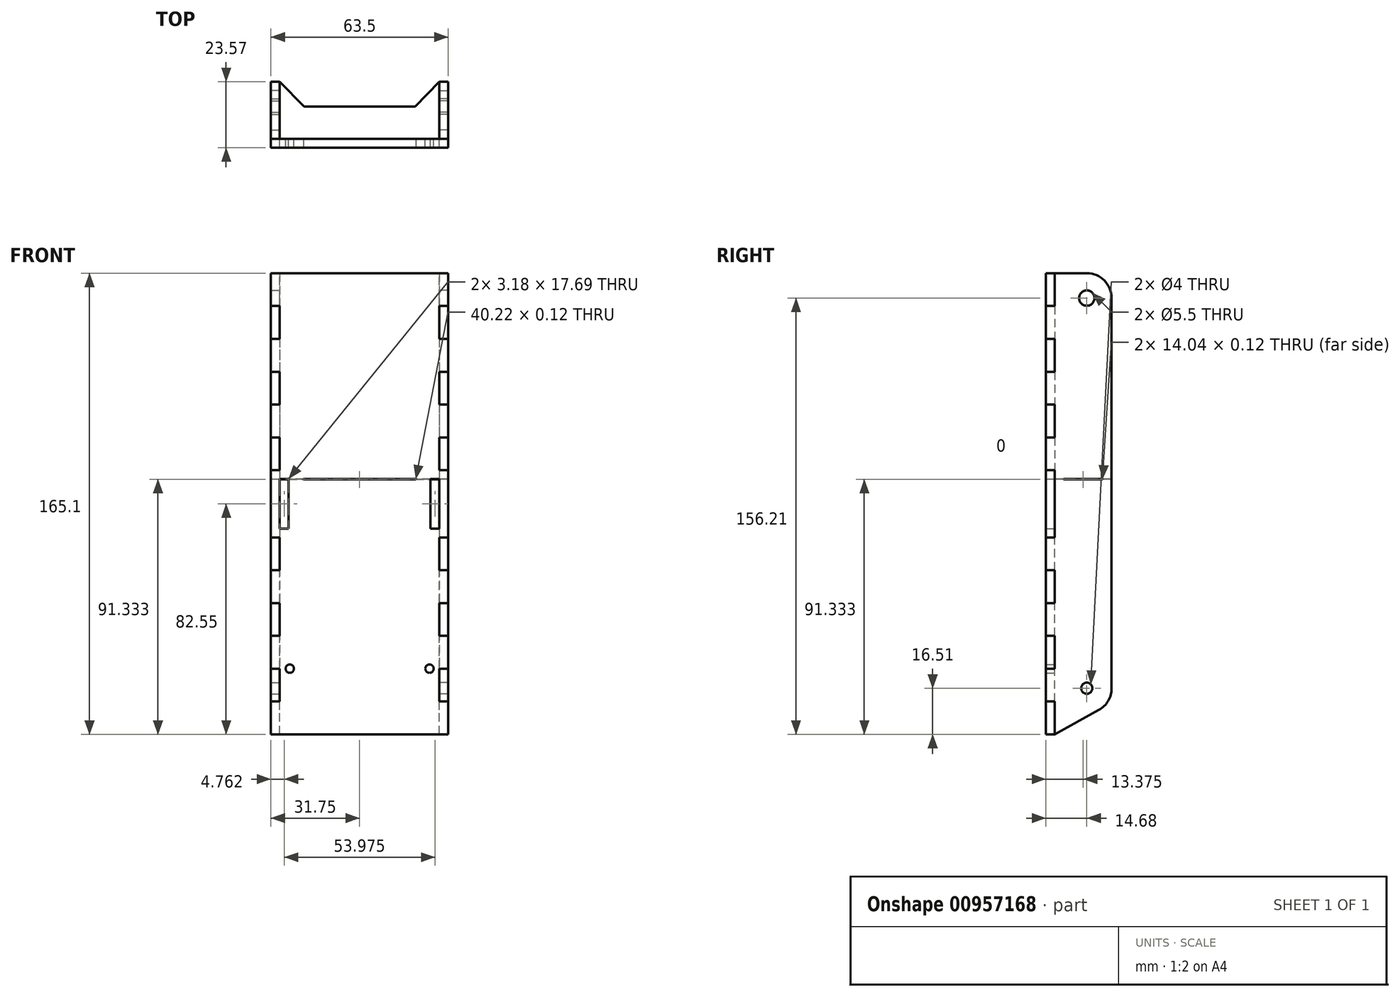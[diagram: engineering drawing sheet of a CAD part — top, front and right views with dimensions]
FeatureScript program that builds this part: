
annotation { "Feature Type Name" : "Feature", "Feature Type Description" : "" }
export const myFeature = defineFeature(function(context is Context, id is Id, definition is map)
    precondition{}
    {
        {
            assignVariable(context, id + "F0", {"name" : "Thickness", "anyValue" : .125});
        }
        {
            var Q0;
            Q0=qCreatedBy(makeId("Front.planeOp"),FACE);
            var sketch = newSketch(context, id + "F1", { "sketchPlane" : qUnion([Q0])});
            skLineSegment(sketch, "E0", {"start": v(0, 0) * mm, "end": v(0, 49.56) * mm, "construction": true});
            skLineSegment(sketch, "E1", {"start": v(0, 0) * mm, "end": v(-25, 0) * mm, "construction": true});
            skCircle(sketch, "E2", {"center": v(-25, 0) * mm, "radius": 1.5 * mm, "construction": true});
            skLineSegment(sketch, "E3", {"start": v(0, -7) * mm, "end": v(-39.83, -7) * mm, "construction": true});
            skLineSegment(sketch, "E4", {"start": v(0, 141.6) * mm, "end": v(-22.22, 141.6) * mm, "construction": true});
            skLineSegment(sketch, "E5", {"start": v(-22.23, 141.6) * mm, "end": v(-22.22, -23.51) * mm, "construction": true});
            skLineSegment(sketch, "E6", {"start": v(-22.22, -23.51) * mm, "end": v(0, -23.5) * mm, "construction": true});
            skSolve(sketch);
        }
        {
            var Q0;
            Q0=qCreatedBy(makeId("Right.planeOp"),FACE);
            var sketch = newSketch(context, id + "F2", { "sketchPlane" : qUnion([Q0])});
            skLineSegment(sketch, "E7", {"start": v(0, -7) * mm, "end": v(11.5, -7) * mm, "construction": true});
            skCircle(sketch, "E8", {"center": v(11.5, -7) * mm, "radius": 2 * mm});
            skCircle(sketch, "E9", {"center": v(11.5, 132.7) * mm, "radius": 2.75 * mm});
            skSolve(sketch);
        }
        {
            var Q0;
            Q0=qCreatedBy(makeId("Front.planeOp"),FACE);
            var sketch = newSketch(context, id + "F3", { "sketchPlane" : qUnion([Q0])});
            skLineSegment(sketch, "E10", {"start": v(0, 141.6) * mm, "end": v(-31.75, 141.6) * mm, "construction": true});
            skLineSegment(sketch, "E11", {"start": v(0, -23.51) * mm, "end": v(-31.75, -23.51) * mm});
            skLineSegment(sketch, "E12", {"start": v(-31.75, -23.51) * mm, "end": v(-31.75, -11.76) * mm});
            skLineSegment(sketch, "E13", {"start": v(-31.75, -11.76) * mm, "end": v(-28.57, -11.76) * mm});
            skLineSegment(sketch, "E14", {"start": v(-28.57, -11.76) * mm, "end": v(-28.57, 0) * mm});
            skLineSegment(sketch, "E15", {"start": v(-28.57, 0) * mm, "end": v(-31.75, 0) * mm});
            skLineSegment(sketch, "E16", {"start": v(0, -23.51) * mm, "end": v(0, 141.6) * mm, "construction": true});
            skLineSegment(sketch, "E17", {"start": v(0, 59.04) * mm, "end": v(-66.34, 59.04) * mm, "construction": true});
            skLineSegment(sketch, "E18", {"start": v(-31.75, 59.04) * mm, "end": v(-31.75, 47.02) * mm});
            skLineSegment(sketch, "E19.1.0.0", {"start": v(-28.57, 23.51) * mm, "end": v(-31.75, 23.51) * mm});
            skLineSegment(sketch, "E19.1.0.1", {"start": v(-28.57, 11.76) * mm, "end": v(-28.57, 23.51) * mm});
            skLineSegment(sketch, "E19.1.0.2", {"start": v(-31.75, 11.76) * mm, "end": v(-28.57, 11.76) * mm});
            skLineSegment(sketch, "E19.1.0.3", {"start": v(-31.75, 0) * mm, "end": v(-31.75, 11.76) * mm});
            skLineSegment(sketch, "E19.2.0.0", {"start": v(-28.58, 47.02) * mm, "end": v(-31.75, 47.02) * mm});
            skLineSegment(sketch, "E19.2.0.1", {"start": v(-28.57, 35.27) * mm, "end": v(-28.57, 47.02) * mm});
            skLineSegment(sketch, "E19.2.0.2", {"start": v(-31.75, 35.27) * mm, "end": v(-28.58, 35.27) * mm});
            skLineSegment(sketch, "E19.2.0.3", {"start": v(-31.75, 23.51) * mm, "end": v(-31.75, 35.27) * mm});
            skLineSegment(sketch, "E19.direction1", {"start": v(-31.75, -23.51) * mm, "end": v(-31.75, 0) * mm, "construction": true});
            skLineSegment(sketch, "E20.MirrorCS", {"start": v(0, 141.6) * mm, "end": v(-31.75, 141.6) * mm});
            skLineSegment(sketch, "E21.MirrorCS", {"start": v(-28.57, 118.08) * mm, "end": v(-31.75, 118.08) * mm});
            skLineSegment(sketch, "E22.MirrorCS", {"start": v(-28.57, 94.57) * mm, "end": v(-31.75, 94.57) * mm});
            skLineSegment(sketch, "E23.MirrorCS", {"start": v(-31.75, 106.33) * mm, "end": v(-28.57, 106.33) * mm});
            skLineSegment(sketch, "E24.MirrorCS", {"start": v(-28.58, 71.06) * mm, "end": v(-31.75, 71.06) * mm});
            skLineSegment(sketch, "E25.MirrorCS", {"start": v(-31.75, 129.84) * mm, "end": v(-28.57, 129.84) * mm});
            skLineSegment(sketch, "E26.MirrorCS", {"start": v(-31.75, 82.81) * mm, "end": v(-28.58, 82.81) * mm});
            skLineSegment(sketch, "E27.MirrorCS", {"start": v(-31.75, 141.6) * mm, "end": v(-31.75, 129.84) * mm});
            skLineSegment(sketch, "E28.MirrorCS", {"start": v(-31.75, 118.08) * mm, "end": v(-31.75, 106.33) * mm});
            skLineSegment(sketch, "E29.MirrorCS", {"start": v(-28.57, 129.84) * mm, "end": v(-28.57, 118.08) * mm});
            skLineSegment(sketch, "E30.MirrorCS", {"start": v(-28.57, 82.81) * mm, "end": v(-28.57, 71.06) * mm});
            skLineSegment(sketch, "E31.MirrorCS", {"start": v(-31.75, 94.57) * mm, "end": v(-31.75, 82.81) * mm});
            skLineSegment(sketch, "E32.MirrorCS", {"start": v(-31.75, 59.04) * mm, "end": v(-31.75, 71.06) * mm});
            skLineSegment(sketch, "E33.MirrorCS", {"start": v(-28.57, 106.33) * mm, "end": v(-28.57, 94.57) * mm});
            skLineSegment(sketch, "E34.bottom", {"start": v(-28.57, 67.89) * mm, "end": v(-25.4, 67.89) * mm});
            skLineSegment(sketch, "E34.top", {"start": v(-28.57, 50.2) * mm, "end": v(-25.4, 50.2) * mm});
            skLineSegment(sketch, "E34.left", {"start": v(-28.57, 67.89) * mm, "end": v(-28.57, 50.2) * mm});
            skLineSegment(sketch, "E34.right", {"start": v(-25.4, 67.89) * mm, "end": v(-25.4, 50.2) * mm});
            skPoint(sketch, "E35", {"position": v(-28.57, 59.04) * mm});
            skLineSegment(sketch, "E36.MirrorCS", {"start": v(0, 141.6) * mm, "end": v(31.75, 141.6) * mm});
            skLineSegment(sketch, "E37.MirrorCS", {"start": v(0, -23.51) * mm, "end": v(31.75, -23.51) * mm});
            skLineSegment(sketch, "E38.MirrorCS", {"start": v(28.57, 0) * mm, "end": v(31.75, 0) * mm});
            skLineSegment(sketch, "E39.MirrorCS", {"start": v(31.75, 59.04) * mm, "end": v(31.75, 71.06) * mm});
            skLineSegment(sketch, "E40.MirrorCS", {"start": v(31.75, 59.04) * mm, "end": v(31.75, 47.02) * mm});
            skLineSegment(sketch, "E41.MirrorCS", {"start": v(28.57, 23.51) * mm, "end": v(31.75, 23.51) * mm});
            skLineSegment(sketch, "E42.MirrorCS", {"start": v(31.75, 11.76) * mm, "end": v(28.57, 11.76) * mm});
            skLineSegment(sketch, "E43.MirrorCS", {"start": v(31.75, 35.27) * mm, "end": v(28.58, 35.27) * mm});
            skLineSegment(sketch, "E44.MirrorCS", {"start": v(28.58, 47.02) * mm, "end": v(31.75, 47.02) * mm});
            skLineSegment(sketch, "E45.MirrorCS", {"start": v(31.75, 82.81) * mm, "end": v(28.58, 82.81) * mm});
            skLineSegment(sketch, "E46.MirrorCS", {"start": v(28.57, 67.89) * mm, "end": v(25.4, 67.89) * mm});
            skLineSegment(sketch, "E47.MirrorCS", {"start": v(31.75, -11.76) * mm, "end": v(28.57, -11.76) * mm});
            skLineSegment(sketch, "E48.MirrorCS", {"start": v(28.57, 94.57) * mm, "end": v(31.75, 94.57) * mm});
            skLineSegment(sketch, "E49.MirrorCS", {"start": v(31.75, 106.33) * mm, "end": v(28.57, 106.33) * mm});
            skLineSegment(sketch, "E50.MirrorCS", {"start": v(28.57, 118.08) * mm, "end": v(31.75, 118.08) * mm});
            skLineSegment(sketch, "E51.MirrorCS", {"start": v(28.58, 71.06) * mm, "end": v(31.75, 71.06) * mm});
            skLineSegment(sketch, "E52.MirrorCS", {"start": v(28.57, 67.89) * mm, "end": v(28.57, 50.2) * mm});
            skLineSegment(sketch, "E53.MirrorCS", {"start": v(28.57, 50.2) * mm, "end": v(25.4, 50.2) * mm});
            skLineSegment(sketch, "E54.MirrorCS", {"start": v(31.75, 129.84) * mm, "end": v(28.57, 129.84) * mm});
            skLineSegment(sketch, "E55.MirrorCS", {"start": v(31.75, -23.51) * mm, "end": v(31.75, -11.76) * mm});
            skLineSegment(sketch, "E56.MirrorCS", {"start": v(31.75, 0) * mm, "end": v(31.75, 11.76) * mm});
            skLineSegment(sketch, "E57.MirrorCS", {"start": v(25.4, 67.89) * mm, "end": v(25.4, 50.2) * mm});
            skLineSegment(sketch, "E58.MirrorCS", {"start": v(31.75, 118.08) * mm, "end": v(31.75, 106.33) * mm});
            skLineSegment(sketch, "E59.MirrorCS", {"start": v(31.75, 94.57) * mm, "end": v(31.75, 82.81) * mm});
            skLineSegment(sketch, "E60.MirrorCS", {"start": v(31.75, 23.51) * mm, "end": v(31.75, 35.27) * mm});
            skLineSegment(sketch, "E61.MirrorCS", {"start": v(28.57, 11.76) * mm, "end": v(28.57, 23.51) * mm});
            skLineSegment(sketch, "E62.MirrorCS", {"start": v(28.57, 82.81) * mm, "end": v(28.57, 71.06) * mm});
            skPoint(sketch, "E63.MirrorP", {"position": v(28.57, 59.04) * mm});
            skLineSegment(sketch, "E64.MirrorCS", {"start": v(28.57, 129.84) * mm, "end": v(28.57, 118.08) * mm});
            skLineSegment(sketch, "E65.MirrorCS", {"start": v(31.75, 141.6) * mm, "end": v(31.75, 129.84) * mm});
            skLineSegment(sketch, "E66.MirrorCS", {"start": v(28.57, 35.27) * mm, "end": v(28.57, 47.02) * mm});
            skLineSegment(sketch, "E67.MirrorCS", {"start": v(28.57, 106.33) * mm, "end": v(28.57, 94.57) * mm});
            skLineSegment(sketch, "E68.MirrorCS", {"start": v(28.57, -11.76) * mm, "end": v(28.57, 0) * mm});
            skCircle(sketch, "E69", {"center": v(-25, 0) * mm, "radius": 1.5 * mm});
            skCircle(sketch, "E70.MirrorC", {"center": v(25, 0) * mm, "radius": 1.5 * mm});
            skSolve(sketch);
        }
        {
            var Q0;
            Q0=makeQuery(id+"F3.imprint","IMPRINT",FACE,{"disambiguationData":[TD([[makeQuery(id+"F3.imprint","IMPRINT",EDGE,{"derivedFrom":sQuery(id+"F3.wireOp",EDGE,"E11")}),-1.0]])]});
            extrude(context, id + "F4", {"entities" : qUnion([Q0]), "depth" : 3.17 * mm, "offsetDistance" : 25.4 * mm});
        }
        {
            var Q0;
            Q0=qCreatedBy(makeId("Right.planeOp"),FACE);
            var sketch = newSketch(context, id + "F5", { "sketchPlane" : qUnion([Q0])});
            skLineSegment(sketch, "E71", {"start": v(0, -23.51) * mm, "end": v(0, -11.76) * mm});
            skLineSegment(sketch, "E72", {"start": v(0, -11.76) * mm, "end": v(-3.18, -11.76) * mm});
            skLineSegment(sketch, "E73", {"start": v(-3.18, -11.76) * mm, "end": v(-3.18, 0) * mm});
            skLineSegment(sketch, "E74", {"start": v(-3.18, 0) * mm, "end": v(0, 0) * mm});
            skLineSegment(sketch, "E75.1.0.0", {"start": v(0, 0) * mm, "end": v(0, 11.76) * mm});
            skLineSegment(sketch, "E75.1.0.1", {"start": v(0, 11.76) * mm, "end": v(-3.18, 11.76) * mm});
            skLineSegment(sketch, "E75.1.0.2", {"start": v(-3.18, 11.76) * mm, "end": v(-3.18, 23.51) * mm});
            skLineSegment(sketch, "E75.1.0.3", {"start": v(-3.18, 23.51) * mm, "end": v(0, 23.51) * mm});
            skLineSegment(sketch, "E75.2.0.0", {"start": v(0, 23.51) * mm, "end": v(0, 35.27) * mm});
            skLineSegment(sketch, "E75.2.0.1", {"start": v(0, 35.27) * mm, "end": v(-3.17, 35.27) * mm});
            skLineSegment(sketch, "E75.2.0.2", {"start": v(-3.17, 35.27) * mm, "end": v(-3.17, 47.02) * mm});
            skLineSegment(sketch, "E75.2.0.3", {"start": v(-3.17, 47.02) * mm, "end": v(0, 47.02) * mm});
            skLineSegment(sketch, "E75.direction1", {"start": v(0, -23.51) * mm, "end": v(0, 0) * mm, "construction": true});
            skLineSegment(sketch, "E76", {"start": v(72.98, 59.04) * mm, "end": v(0, 59.04) * mm, "construction": true});
            skLineSegment(sketch, "E77", {"start": v(0, 47.02) * mm, "end": v(0, 59.04) * mm});
            skLineSegment(sketch, "E78.MirrorCS", {"start": v(0, 141.6) * mm, "end": v(0, 129.84) * mm});
            skLineSegment(sketch, "E79.MirrorCS", {"start": v(0, 129.84) * mm, "end": v(-3.18, 129.84) * mm});
            skLineSegment(sketch, "E80.MirrorCS", {"start": v(-3.18, 129.84) * mm, "end": v(-3.18, 118.08) * mm});
            skLineSegment(sketch, "E81.MirrorCS", {"start": v(-3.18, 118.08) * mm, "end": v(0, 118.08) * mm});
            skLineSegment(sketch, "E82.MirrorCS", {"start": v(0, 106.33) * mm, "end": v(-3.18, 106.33) * mm});
            skLineSegment(sketch, "E83.MirrorCS", {"start": v(-3.18, 94.57) * mm, "end": v(0, 94.57) * mm});
            skLineSegment(sketch, "E84.MirrorCS", {"start": v(-3.18, 106.33) * mm, "end": v(-3.18, 94.57) * mm});
            skLineSegment(sketch, "E85.MirrorCS", {"start": v(-3.17, 71.06) * mm, "end": v(0, 71.06) * mm});
            skLineSegment(sketch, "E86.MirrorCS", {"start": v(0, 71.06) * mm, "end": v(0, 59.04) * mm});
            skLineSegment(sketch, "E87.MirrorCS", {"start": v(0, 94.57) * mm, "end": v(0, 82.81) * mm});
            skLineSegment(sketch, "E88.MirrorCS", {"start": v(0, 82.81) * mm, "end": v(-3.18, 82.81) * mm});
            skLineSegment(sketch, "E89.MirrorCS", {"start": v(-3.18, 82.81) * mm, "end": v(-3.17, 71.06) * mm});
            skLineSegment(sketch, "E90.MirrorCS", {"start": v(0, 118.08) * mm, "end": v(0, 106.33) * mm});
            skPoint(sketch, "E91.endSnap0", {"position": v(0, -17.63) * mm});
            skLineSegment(sketch, "E92", {"start": v(0, 141.6) * mm, "end": v(11.5, 141.6) * mm});
            skLineSegment(sketch, "E93", {"start": v(11.5, 141.6) * mm, "end": v(1.97, 141.6) * mm});
            skLineSegment(sketch, "E94", {"start": v(1.97, 141.6) * mm, "end": v(0, 141.6) * mm});
            skPoint(sketch, "E95.startSnap0", {"position": v(0, 135.71) * mm});
            skCircle(sketch, "E96", {"center": v(11.5, 132.7) * mm, "radius": 2.75 * mm});
            skLineSegment(sketch, "E97", {"start": v(20.39, 132.7) * mm, "end": v(20.4, -7) * mm});
            skArc(sketch, "E98", {"start": v(11.5, 141.6) * mm, "mid": v(17.79, 138.99) * mm, "end": v(20.39, 132.7) * mm});
            skLineSegment(sketch, "E99", {"start": v(0, -23.51) * mm, "end": v(15.8, -14.78) * mm});
            skArc(sketch, "E100", {"start": v(20.4, -7) * mm, "mid": v(19.16, -11.52) * mm, "end": v(15.8, -14.78) * mm});
            skCircle(sketch, "E101", {"center": v(11.5, -7) * mm, "radius": 2 * mm});
            skSolve(sketch);
        }
        {
            var Q0;
            Q0=makeQuery(id+"F5.imprint","IMPRINT",FACE,{"disambiguationData":[TD([[makeQuery(id+"F5.imprint","IMPRINT",EDGE,{"derivedFrom":sQuery(id+"F5.wireOp",EDGE,"E71")}),-1.0]])]});
            var Q1;
            Q1=makeQuery(id+"F4.opExtrude","CAP_VERTEX",VERTEX,{"disambiguationData":[OSD([sQuery(id+"F3.wireOp",EDGE,"E36.MirrorCS"),sQuery(id+"F3.wireOp",EDGE,"E65.MirrorCS")])],"isStart":true});
            var Q2;
            Q2=makeQuery(id+"F4.opExtrude","CAP_VERTEX",VERTEX,{"disambiguationData":[OSD([sQuery(id+"F3.wireOp",EDGE,"E54.MirrorCS"),sQuery(id+"F3.wireOp",EDGE,"E64.MirrorCS")])],"isStart":true});
            extrude(context, id + "F6", {"entities" : qUnion([Q0]), "endBound" : BoundingType.UP_TO_VERTEX, "depth" : 25.4 * mm, "endBoundEntityVertex" : qUnion([Q1]), "offsetDistance" : 25.4 * mm, "hasSecondDirection" : true, "secondDirectionBound" : SecondDirectionBoundingType.UP_TO_VERTEX, "secondDirectionOppositeDirection" : false, "secondDirectionDepth" : 25.4 * mm, "secondDirectionBoundEntityVertex" : qUnion([Q2])});
        }
        {
            var Q0;
            Q0=makeQuery(id+"F6.opExtrude","SWEPT_BODY",BODY,{"disambiguationData":[OSD([sQuery(id+"F5.wireOp",EDGE,"E71"),sQuery(id+"F5.wireOp",EDGE,"E72"),sQuery(id+"F5.wireOp",EDGE,"E73"),sQuery(id+"F5.wireOp",EDGE,"E74"),sQuery(id+"F5.wireOp",EDGE,"E75.1.0.0"),sQuery(id+"F5.wireOp",EDGE,"E75.1.0.1"),sQuery(id+"F5.wireOp",EDGE,"E75.1.0.2"),sQuery(id+"F5.wireOp",EDGE,"E75.1.0.3"),sQuery(id+"F5.wireOp",EDGE,"E75.2.0.0"),sQuery(id+"F5.wireOp",EDGE,"E75.2.0.1"),sQuery(id+"F5.wireOp",EDGE,"E75.2.0.2"),sQuery(id+"F5.wireOp",EDGE,"E75.2.0.3"),sQuery(id+"F5.wireOp",EDGE,"E77"),sQuery(id+"F5.wireOp",EDGE,"E78.MirrorCS"),sQuery(id+"F5.wireOp",EDGE,"E79.MirrorCS"),sQuery(id+"F5.wireOp",EDGE,"E80.MirrorCS"),sQuery(id+"F5.wireOp",EDGE,"E81.MirrorCS"),sQuery(id+"F5.wireOp",EDGE,"E82.MirrorCS"),sQuery(id+"F5.wireOp",EDGE,"E83.MirrorCS"),sQuery(id+"F5.wireOp",EDGE,"E84.MirrorCS"),sQuery(id+"F5.wireOp",EDGE,"E85.MirrorCS"),sQuery(id+"F5.wireOp",EDGE,"E86.MirrorCS"),sQuery(id+"F5.wireOp",EDGE,"E87.MirrorCS"),sQuery(id+"F5.wireOp",EDGE,"E88.MirrorCS"),sQuery(id+"F5.wireOp",EDGE,"E89.MirrorCS"),sQuery(id+"F5.wireOp",EDGE,"E90.MirrorCS"),sQuery(id+"F5.wireOp",EDGE,"E93"),sQuery(id+"F5.wireOp",EDGE,"E94"),sQuery(id+"F5.wireOp",EDGE,"E96"),sQuery(id+"F5.wireOp",EDGE,"E97"),sQuery(id+"F5.wireOp",EDGE,"E98"),sQuery(id+"F5.wireOp",EDGE,"E99"),sQuery(id+"F5.wireOp",EDGE,"E100"),sQuery(id+"F5.wireOp",EDGE,"E101")])]});
            var Q1;
            Q1=qCreatedBy(makeId("Right.planeOp"),FACE);
            mirror(context, id + "F7", {"entities" : qUnion([Q0]), "mirrorPlane" : qUnion([Q1])});
        }
        {
            var Q0;
            Q0=qCreatedBy(makeId("Top.planeOp"),FACE);
            var sketch = newSketch(context, id + "F8", { "sketchPlane" : qUnion([Q0])});
            skLineSegment(sketch, "E102", {"start": v(0, 11.5) * mm, "end": v(-19.91, 11.5) * mm});
            skLineSegment(sketch, "E103", {"start": v(-19.91, 11.5) * mm, "end": v(-28.57, 20.39) * mm});
            skLineSegment(sketch, "E104", {"start": v(-28.57, 20.39) * mm, "end": v(-28.57, 17.21) * mm});
            skLineSegment(sketch, "E105", {"start": v(-28.57, 17.21) * mm, "end": v(-31.75, 17.21) * mm});
            skLineSegment(sketch, "E106", {"start": v(-31.75, 17.21) * mm, "end": v(-31.75, 3.17) * mm});
            skLineSegment(sketch, "E107", {"start": v(-31.75, 3.17) * mm, "end": v(-28.57, 3.18) * mm});
            skLineSegment(sketch, "E108", {"start": v(-28.57, 0) * mm, "end": v(-20.1, 0) * mm});
            skLineSegment(sketch, "E109", {"start": v(-20.1, 0) * mm, "end": v(-20.1, -3.18) * mm});
            skLineSegment(sketch, "E110", {"start": v(-20.1, -3.18) * mm, "end": v(0, -3.18) * mm});
            skLineSegment(sketch, "E111", {"start": v(0, -3.18) * mm, "end": v(0, 11.5) * mm, "construction": true});
            skLineSegment(sketch, "E112", {"start": v(-28.57, 3.18) * mm, "end": v(-28.57, 0) * mm});
            skLineSegment(sketch, "E113.MirrorCS", {"start": v(20.1, -3.18) * mm, "end": v(0, -3.18) * mm});
            skLineSegment(sketch, "E114.MirrorCS", {"start": v(0, 11.5) * mm, "end": v(19.91, 11.5) * mm});
            skLineSegment(sketch, "E115.MirrorCS", {"start": v(20.1, 0) * mm, "end": v(20.1, -3.17) * mm});
            skLineSegment(sketch, "E116.MirrorCS", {"start": v(28.57, 3.18) * mm, "end": v(28.57, 0) * mm});
            skLineSegment(sketch, "E117.MirrorCS", {"start": v(28.57, 20.4) * mm, "end": v(28.57, 17.22) * mm});
            skLineSegment(sketch, "E118.MirrorCS", {"start": v(31.75, 3.17) * mm, "end": v(28.57, 3.18) * mm});
            skLineSegment(sketch, "E119.MirrorCS", {"start": v(28.57, 17.21) * mm, "end": v(31.75, 17.21) * mm});
            skLineSegment(sketch, "E120.MirrorCS", {"start": v(28.57, 0) * mm, "end": v(20.1, 0) * mm});
            skLineSegment(sketch, "E121.MirrorCS", {"start": v(31.75, 17.22) * mm, "end": v(31.75, 3.18) * mm});
            skLineSegment(sketch, "E122.MirrorCS", {"start": v(19.91, 11.5) * mm, "end": v(28.57, 20.4) * mm});
            skSolve(sketch);
        }
        {
            var Q0;
            Q0 = qSketchRegion(id + "F8", true);
            var Q1;
            Q1=makeQuery(id+"F4.opExtrude","CAP_VERTEX",VERTEX,{"disambiguationData":[OSD([sQuery(id+"F3.wireOp",EDGE,"E34.bottom"),sQuery(id+"F3.wireOp",EDGE,"E34.right")])],"isStart":true});
            var Q2;
            Q2=makeQuery(id+"F4.opExtrude","CAP_VERTEX",VERTEX,{"disambiguationData":[OSD([sQuery(id+"F3.wireOp",EDGE,"E34.bottom"),sQuery(id+"F3.wireOp",EDGE,"E34.right")])],"isStart":true});
            extrude(context, id + "F9", {"entities" : qUnion([Q0]), "operationType" : NewBodyOperationType.REMOVE, "endBound" : BoundingType.UP_TO_VERTEX, "depth" : 25.4 * mm, "endBoundEntityVertex" : qUnion([Q1]), "offsetDistance" : 25.4 * mm, "hasSecondDirection" : true, "secondDirectionBound" : SecondDirectionBoundingType.UP_TO_VERTEX, "secondDirectionOppositeDirection" : false, "secondDirectionDepth" : 25.4 * mm, "secondDirectionBoundEntityVertex" : qUnion([Q2]), "hasSecondDirectionOffset" : true, "secondDirectionOffsetDistance" : (getVariable(context, 'Thickness')) * mm});
        }
        {
            var Q0;
            Q0 = qSketchRegion(id + "F8", true);
            var Q1;
            Q1=makeQuery(id+"F9.boolean.opBoolean","COPY",VERTEX,{"derivedFrom":makeQuery(id+"F9.opExtrude","CAP_VERTEX",VERTEX,{"disambiguationData":[OSD([sQuery(id+"F8.wireOp",EDGE,"E108"),sQuery(id+"F8.wireOp",EDGE,"E109")])],"isStart":false})});
            var Q2;
            Q2=makeQuery(id+"F9.boolean.opBoolean","COPY",VERTEX,{"derivedFrom":makeQuery(id+"F9.opExtrude","CAP_VERTEX",VERTEX,{"disambiguationData":[OSD([sQuery(id+"F8.wireOp",EDGE,"E108"),sQuery(id+"F8.wireOp",EDGE,"E109")])],"isStart":true})});
            extrude(context, id + "F10", {"entities" : qUnion([Q0]), "endBound" : BoundingType.UP_TO_VERTEX, "depth" : 25.4 * mm, "endBoundEntityVertex" : qUnion([Q1]), "offsetDistance" : 25.4 * mm, "hasSecondDirection" : true, "secondDirectionBound" : SecondDirectionBoundingType.UP_TO_VERTEX, "secondDirectionOppositeDirection" : false, "secondDirectionDepth" : 25.4 * mm, "secondDirectionBoundEntityVertex" : qUnion([Q2])});
        }
    });
